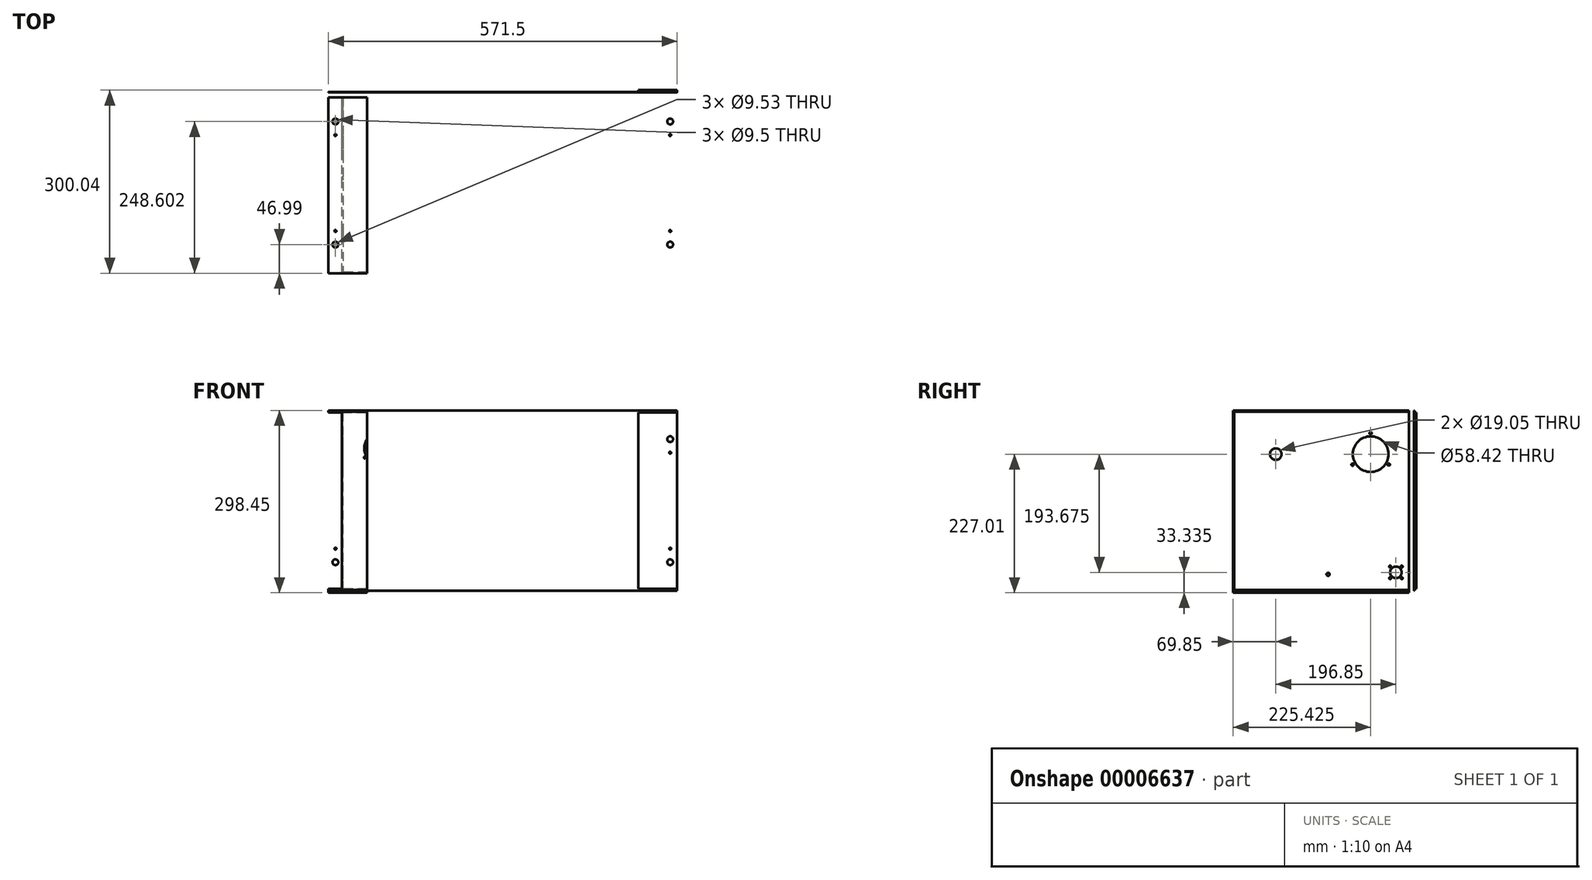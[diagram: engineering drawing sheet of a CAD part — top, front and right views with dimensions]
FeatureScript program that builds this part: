
annotation { "Feature Type Name" : "Feature", "Feature Type Description" : "" }
export const myFeature = defineFeature(function(context is Context, id is Id, definition is map)
    precondition{}
    {
        {
            var Q0;
            Q0=qCreatedBy(makeId("Top.planeOp"),FACE);
            var sketch = newSketch(context, id + "F0", { "sketchPlane" : qUnion([Q0])});
            skLineSegment(sketch, "E0", {"start": v(-263.53, 0) * mm, "end": v(263.53, 0) * mm});
            skLineSegment(sketch, "E1", {"start": v(-263.53, 0) * mm, "end": v(-263.53, 295.28) * mm});
            skLineSegment(sketch, "E2", {"start": v(-263.53, 295.28) * mm, "end": v(-262, 295.28) * mm});
            skLineSegment(sketch, "E3", {"start": v(-262, 295.28) * mm, "end": v(-262, 1.52) * mm});
            skLineSegment(sketch, "E4", {"start": v(-262, 1.52) * mm, "end": v(0, 1.52) * mm});
            skLineSegment(sketch, "E5", {"start": v(0, -110.06) * mm, "end": v(0, 345.42) * mm, "construction": true});
            skLineSegment(sketch, "E6.0.MirrorCS", {"start": v(262, 295.28) * mm, "end": v(262, 1.52) * mm});
            skLineSegment(sketch, "E6.1.MirrorCS", {"start": v(263.53, 0) * mm, "end": v(263.53, 295.28) * mm});
            skLineSegment(sketch, "E6.2.MirrorCS", {"start": v(262, 1.52) * mm, "end": v(0, 1.52) * mm});
            skLineSegment(sketch, "E6.3.MirrorCS", {"start": v(263.53, 295.28) * mm, "end": v(262, 295.28) * mm});
            skSolve(sketch);
        }
        {
            var Q0;
            Q0=makeQuery(id+"F0.imprint","IMPRINT",FACE,{"disambiguationData":[TD([[makeQuery(id+"F0.imprint","IMPRINT",EDGE,{"derivedFrom":sQuery(id+"F0.wireOp",EDGE,"E0")}),1.0]])]});
            var Q1;
            Q1=sQuery(id+"F0.wireOp",EDGE,"E3");
            extrude(context, id + "F1", {"entities" : qUnion([Q0]), "surfaceEntities" : qUnion([Q1]), "depth" : 292.1 * mm});
        }
        {
            var Q0;
            Q0=makeQuery(id+"F1.opExtrude","SWEPT_EDGE",EDGE,{"disambiguationData":[OSD([sQuery(id+"F0.wireOp",EDGE,"E0"),sQuery(id+"F0.wireOp",EDGE,"E1")])]});
            var Q1;
            Q1=makeQuery(id+"F1.opExtrude","CAP_EDGE",EDGE,{"disambiguationData":[OSD([sQuery(id+"F0.wireOp",EDGE,"E0")])],"isStart":true});
            var Q2;
            Q2=makeQuery(id+"F1.opExtrude","CAP_EDGE",EDGE,{"disambiguationData":[OSD([sQuery(id+"F0.wireOp",EDGE,"E1")])],"isStart":true});
            var Q3;
            Q3=makeQuery(id+"F1.opExtrude","SWEPT_EDGE",EDGE,{"disambiguationData":[OSD([sQuery(id+"F0.wireOp",EDGE,"E1"),sQuery(id+"F0.wireOp",EDGE,"E2")])]});
            var Q4;
            Q4=makeQuery(id+"F1.opExtrude","CAP_EDGE",EDGE,{"disambiguationData":[OSD([sQuery(id+"F0.wireOp",EDGE,"E1")])],"isStart":false});
            var Q5;
            Q5=makeQuery(id+"F1.opExtrude","CAP_EDGE",EDGE,{"disambiguationData":[OSD([sQuery(id+"F0.wireOp",EDGE,"E0")])],"isStart":false});
            var Q6;
            Q6=makeQuery(id+"F1.opExtrude","SWEPT_EDGE",EDGE,{"disambiguationData":[OSD([sQuery(id+"F0.wireOp",EDGE,"E0"),sQuery(id+"F0.wireOp",EDGE,"E6.1.MirrorCS")])]});
            var Q7;
            Q7=makeQuery(id+"F1.opExtrude","CAP_EDGE",EDGE,{"disambiguationData":[OSD([sQuery(id+"F0.wireOp",EDGE,"E6.1.MirrorCS")])],"isStart":false});
            var Q8;
            Q8=makeQuery(id+"F1.opExtrude","SWEPT_EDGE",EDGE,{"disambiguationData":[OSD([sQuery(id+"F0.wireOp",EDGE,"E6.1.MirrorCS"),sQuery(id+"F0.wireOp",EDGE,"E6.3.MirrorCS")])]});
            var Q9;
            Q9=makeQuery(id+"F1.opExtrude","CAP_EDGE",EDGE,{"disambiguationData":[OSD([sQuery(id+"F0.wireOp",EDGE,"E6.1.MirrorCS")])],"isStart":true});
            fillet(context, id + "F2", {"entities" : qUnion([Q0, Q1, Q2, Q3, Q4, Q5, Q6, Q7, Q8, Q9]), "radius" : 1.27 * mm, "tangentPropagation" : true, "allowEdgeOverflow" : false});
        }
        {
            var Q0;
            Q0=makeQuery(id+"F1.opExtrude","SWEPT_FACE",FACE,{"disambiguationData":[OSD([sQuery(id+"F0.wireOp",EDGE,"E0")])]});
            var sketch = newSketch(context, id + "F3", { "sketchPlane" : qUnion([Q0])});
            skLineSegment(sketch, "E7", {"start": v(0, -22.71) * mm, "end": v(0, 428.97) * mm, "construction": true});
            skLineSegment(sketch, "E8", {"start": v(-397, 0) * mm, "end": v(381.47, 0) * mm, "construction": true});
            skLineSegment(sketch, "E9", {"start": v(-394.87, 98.43) * mm, "end": v(382.18, 98.43) * mm, "construction": true});
            skLineSegment(sketch, "E10", {"start": v(-317.78, 107.95) * mm, "end": v(297.56, 107.95) * mm, "construction": true});
            skLineSegment(sketch, "E11", {"start": v(-291.05, 196.85) * mm, "end": v(299.62, 196.85) * mm, "construction": true});
            skLineSegment(sketch, "E12", {"start": v(-305.21, 231.77) * mm, "end": v(297.58, 231.78) * mm, "construction": true});
            skLineSegment(sketch, "E13", {"start": v(-200.02, 339.47) * mm, "end": v(-200.02, -33.8) * mm, "construction": true});
            skLineSegment(sketch, "E14", {"start": v(-161.92, 338.18) * mm, "end": v(-161.92, -31.85) * mm, "construction": true});
            skLineSegment(sketch, "E15", {"start": v(-122.24, 325.89) * mm, "end": v(-122.24, -26.68) * mm, "construction": true});
            skLineSegment(sketch, "E16", {"start": v(-66.68, 340.76) * mm, "end": v(-66.67, -29.91) * mm, "construction": true});
            skLineSegment(sketch, "E17", {"start": v(25.4, 334.3) * mm, "end": v(25.4, -17.62) * mm, "construction": true});
            skLineSegment(sketch, "E18", {"start": v(152.4, 322) * mm, "end": v(152.4, -46.73) * mm, "construction": true});
            skLineSegment(sketch, "E19", {"start": v(263.52, 358.39) * mm, "end": v(263.52, -46.4) * mm, "construction": true});
            skCircle(sketch, "E20", {"center": v(-200.02, 231.77) * mm, "radius": 26.99 * mm});
            skCircle(sketch, "E21", {"center": v(-200.02, 231.77) * mm, "radius": 30.16 * mm, "construction": true});
            skCircle(sketch, "E22", {"center": v(-200.02, 261.94) * mm, "radius": 1.63 * mm});
            skCircle(sketch, "E23.1.0", {"center": v(-226.15, 216.7) * mm, "radius": 1.63 * mm});
            skCircle(sketch, "E23.2.0", {"center": v(-173.9, 216.7) * mm, "radius": 1.63 * mm});
            skCircle(sketch, "E24", {"center": v(-161.92, 98.43) * mm, "radius": 3.18 * mm});
            skCircle(sketch, "E25", {"center": v(-122.24, 98.43) * mm, "radius": 3.18 * mm});
            skCircle(sketch, "E26", {"center": v(-66.68, 196.85) * mm, "radius": 3.18 * mm});
            skCircle(sketch, "E27", {"center": v(25.4, 107.95) * mm, "radius": 3.18 * mm});
            skCircle(sketch, "E28", {"center": v(152.4, 196.85) * mm, "radius": 3.18 * mm});
            skSolve(sketch);
        }
        {
            var Q0;
            Q0=makeQuery(id+"F3.imprint","IMPRINT",FACE,{"disambiguationData":[TD([[makeQuery(id+"F3.imprint","IMPRINT",EDGE,{"derivedFrom":sQuery(id+"F3.wireOp",EDGE,"E22")}),1.0]])]});
            var Q1;
            Q1=makeQuery(id+"F3.imprint","IMPRINT",FACE,{"disambiguationData":[TD([[makeQuery(id+"F3.imprint","IMPRINT",EDGE,{"derivedFrom":sQuery(id+"F3.wireOp",EDGE,"E20")}),1.0]])]});
            var Q2;
            Q2=makeQuery(id+"F3.imprint","IMPRINT",FACE,{"disambiguationData":[TD([[makeQuery(id+"F3.imprint","IMPRINT",EDGE,{"derivedFrom":sQuery(id+"F3.wireOp",EDGE,"E23.1.0")}),1.0]])]});
            var Q3;
            Q3=makeQuery(id+"F3.imprint","IMPRINT",FACE,{"disambiguationData":[TD([[makeQuery(id+"F3.imprint","IMPRINT",EDGE,{"derivedFrom":sQuery(id+"F3.wireOp",EDGE,"E23.2.0")}),1.0]])]});
            var Q4;
            Q4=makeQuery(id+"F3.imprint","IMPRINT",FACE,{"disambiguationData":[TD([[makeQuery(id+"F3.imprint","IMPRINT",EDGE,{"derivedFrom":sQuery(id+"F3.wireOp",EDGE,"E26")}),1.0]])]});
            var Q5;
            Q5=makeQuery(id+"F3.imprint","IMPRINT",FACE,{"disambiguationData":[TD([[makeQuery(id+"F3.imprint","IMPRINT",EDGE,{"derivedFrom":sQuery(id+"F3.wireOp",EDGE,"E24")}),1.0]])]});
            var Q6;
            Q6=makeQuery(id+"F3.imprint","IMPRINT",FACE,{"disambiguationData":[TD([[makeQuery(id+"F3.imprint","IMPRINT",EDGE,{"derivedFrom":sQuery(id+"F3.wireOp",EDGE,"E25")}),1.0]])]});
            var Q7;
            Q7=makeQuery(id+"F3.imprint","IMPRINT",FACE,{"disambiguationData":[TD([[makeQuery(id+"F3.imprint","IMPRINT",EDGE,{"derivedFrom":sQuery(id+"F3.wireOp",EDGE,"E27")}),1.0]])]});
            var Q8;
            Q8=makeQuery(id+"F3.imprint","IMPRINT",FACE,{"disambiguationData":[TD([[makeQuery(id+"F3.imprint","IMPRINT",EDGE,{"derivedFrom":sQuery(id+"F3.wireOp",EDGE,"E28")}),1.0]])]});
            extrude(context, id + "F4", {"entities" : qUnion([Q0, Q1, Q2, Q3, Q4, Q5, Q6, Q7, Q8]), "operationType" : NewBodyOperationType.REMOVE, "oppositeDirection" : true, "depth" : 5.08 * mm});
        }
        {
            var Q0;
            Q0=makeQuery(id+"F1.opExtrude","SWEPT_FACE",FACE,{"disambiguationData":[OSD([sQuery(id+"F0.wireOp",EDGE,"E1")])]});
            var sketch = newSketch(context, id + "F5", { "sketchPlane" : qUnion([Q0])});
            skLineSegment(sketch, "E29", {"start": v(-69.85, 280.52) * mm, "end": v(-69.85, -27.41) * mm, "construction": true});
            skLineSegment(sketch, "E30", {"start": v(-155.58, 281.42) * mm, "end": v(-155.58, -27.41) * mm, "construction": true});
            skLineSegment(sketch, "E31", {"start": v(-225.42, 273.8) * mm, "end": v(-225.42, -23.83) * mm, "construction": true});
            skLineSegment(sketch, "E32", {"start": v(-266.7, 273.35) * mm, "end": v(-266.7, -23.83) * mm, "construction": true});
            skLineSegment(sketch, "E33", {"start": v(-314.98, 222.25) * mm, "end": v(77.22, 222.25) * mm, "construction": true});
            skLineSegment(sketch, "E34", {"start": v(-285.84, 28.57) * mm, "end": v(55.7, 28.57) * mm, "construction": true});
            skLineSegment(sketch, "E35", {"start": v(-279.57, 25.4) * mm, "end": v(62.43, 25.4) * mm, "construction": true});
            skLineSegment(sketch, "E36", {"start": v(-294.95, 0) * mm, "end": v(40.89, 0) * mm, "construction": true});
            skLineSegment(sketch, "E37", {"start": v(0, -20.23) * mm, "end": v(0, 311.99) * mm, "construction": true});
            skCircle(sketch, "E38", {"center": v(-225.42, 222.25) * mm, "radius": 29.21 * mm});
            skCircle(sketch, "E39", {"center": v(-69.85, 222.25) * mm, "radius": 9.53 * mm});
            skCircle(sketch, "E40", {"center": v(-155.58, 25.4) * mm, "radius": 2.54 * mm});
            skCircle(sketch, "E41", {"center": v(-266.7, 28.57) * mm, "radius": 9.53 * mm});
            skCircle(sketch, "E42", {"center": v(-257.18, 38.1) * mm, "radius": 1.63 * mm});
            skCircle(sketch, "E43.0.1.0", {"center": v(-257.18, 19.05) * mm, "radius": 1.63 * mm});
            skCircle(sketch, "E43.1.0.0", {"center": v(-276.23, 38.1) * mm, "radius": 1.63 * mm});
            skCircle(sketch, "E43.1.1.0", {"center": v(-276.23, 19.05) * mm, "radius": 1.63 * mm});
            skLineSegment(sketch, "E43.direction1", {"start": v(-257.18, 38.1) * mm, "end": v(-276.23, 38.1) * mm, "construction": true});
            skLineSegment(sketch, "E43.direction2", {"start": v(-257.18, 38.1) * mm, "end": v(-257.18, 19.05) * mm, "construction": true});
            skCircle(sketch, "E44", {"center": v(-225.43, 256.54) * mm, "radius": 1.9 * mm});
            skCircle(sketch, "E45.1.0", {"center": v(-255.12, 205.1) * mm, "radius": 1.9 * mm});
            skCircle(sketch, "E45.2.0", {"center": v(-195.73, 205.1) * mm, "radius": 1.9 * mm});
            skSolve(sketch);
        }
        {
            var Q0;
            Q0=makeQuery(id+"F5.imprint","IMPRINT",FACE,{"disambiguationData":[TD([[makeQuery(id+"F5.imprint","IMPRINT",EDGE,{"derivedFrom":sQuery(id+"F5.wireOp",EDGE,"E44")}),1.0]])]});
            var Q1;
            Q1=makeQuery(id+"F5.imprint","IMPRINT",FACE,{"disambiguationData":[TD([[makeQuery(id+"F5.imprint","IMPRINT",EDGE,{"derivedFrom":sQuery(id+"F5.wireOp",EDGE,"E38")}),1.0]])]});
            var Q2;
            Q2=makeQuery(id+"F5.imprint","IMPRINT",FACE,{"disambiguationData":[TD([[makeQuery(id+"F5.imprint","IMPRINT",EDGE,{"derivedFrom":sQuery(id+"F5.wireOp",EDGE,"E45.1.0")}),1.0]])]});
            var Q3;
            Q3=makeQuery(id+"F5.imprint","IMPRINT",FACE,{"disambiguationData":[TD([[makeQuery(id+"F5.imprint","IMPRINT",EDGE,{"derivedFrom":sQuery(id+"F5.wireOp",EDGE,"E45.2.0")}),1.0]])]});
            var Q4;
            Q4=makeQuery(id+"F5.imprint","IMPRINT",FACE,{"disambiguationData":[TD([[makeQuery(id+"F5.imprint","IMPRINT",EDGE,{"derivedFrom":sQuery(id+"F5.wireOp",EDGE,"E39")}),1.0]])]});
            var Q5;
            Q5=makeQuery(id+"F5.imprint","IMPRINT",FACE,{"disambiguationData":[TD([[makeQuery(id+"F5.imprint","IMPRINT",EDGE,{"derivedFrom":sQuery(id+"F5.wireOp",EDGE,"E40")}),1.0]])]});
            var Q6;
            Q6=makeQuery(id+"F5.imprint","IMPRINT",FACE,{"disambiguationData":[TD([[makeQuery(id+"F5.imprint","IMPRINT",EDGE,{"derivedFrom":sQuery(id+"F5.wireOp",EDGE,"E41")}),1.0]])]});
            var Q7;
            Q7=makeQuery(id+"F5.imprint","IMPRINT",FACE,{"disambiguationData":[TD([[makeQuery(id+"F5.imprint","IMPRINT",EDGE,{"derivedFrom":sQuery(id+"F5.wireOp",EDGE,"E43.1.0.0")}),1.0]])]});
            var Q8;
            Q8=makeQuery(id+"F5.imprint","IMPRINT",FACE,{"disambiguationData":[TD([[makeQuery(id+"F5.imprint","IMPRINT",EDGE,{"derivedFrom":sQuery(id+"F5.wireOp",EDGE,"E43.1.1.0")}),1.0]])]});
            var Q9;
            Q9=makeQuery(id+"F5.imprint","IMPRINT",FACE,{"disambiguationData":[TD([[makeQuery(id+"F5.imprint","IMPRINT",EDGE,{"derivedFrom":sQuery(id+"F5.wireOp",EDGE,"E43.0.1.0")}),1.0]])]});
            var Q10;
            Q10=makeQuery(id+"F5.imprint","IMPRINT",FACE,{"disambiguationData":[TD([[makeQuery(id+"F5.imprint","IMPRINT",EDGE,{"derivedFrom":sQuery(id+"F5.wireOp",EDGE,"E42")}),1.0]])]});
            extrude(context, id + "F6", {"entities" : qUnion([Q0, Q1, Q2, Q3, Q4, Q5, Q6, Q7, Q8, Q9, Q10]), "operationType" : NewBodyOperationType.REMOVE, "oppositeDirection" : true, "depth" : 5.08 * mm});
        }
        {
            var Q0;
            Q0=makeQuery(id+"F1.opExtrude","SWEPT_FACE",FACE,{"disambiguationData":[OSD([sQuery(id+"F0.wireOp",EDGE,"E6.1.MirrorCS")])]});
            var sketch = newSketch(context, id + "F7", { "sketchPlane" : qUnion([Q0])});
            skLineSegment(sketch, "E46", {"start": v(-61.82, 0) * mm, "end": v(412.73, 0) * mm, "construction": true});
            skLineSegment(sketch, "E47", {"start": v(0, -19.8) * mm, "end": v(0, 392.1) * mm, "construction": true});
            skLineSegment(sketch, "E48", {"start": v(-42.4, 193.68) * mm, "end": v(431.33, 193.68) * mm, "construction": true});
            skLineSegment(sketch, "E49", {"start": v(-58.3, 38.1) * mm, "end": v(354.8, 38.1) * mm, "construction": true});
            skLineSegment(sketch, "E50", {"start": v(34.92, 306) * mm, "end": v(34.93, -19.24) * mm, "construction": true});
            skLineSegment(sketch, "E51", {"start": v(107.95, 307.86) * mm, "end": v(107.95, -22.5) * mm, "construction": true});
            skLineSegment(sketch, "E52", {"start": v(171.45, 313.59) * mm, "end": v(171.45, -34.35) * mm, "construction": true});
            skArc(sketch, "E53", {"start": v(107.95, 257.18) * mm, "mid": v(44.45, 193.68) * mm, "end": v(107.95, 130.18) * mm});
            skCircle(sketch, "E54", {"center": v(34.93, 38.1) * mm, "radius": 7.94 * mm});
            skCircle(sketch, "E55", {"center": v(44.13, 47.3) * mm, "radius": 1.63 * mm});
            skCircle(sketch, "E56.0.1.0", {"center": v(44.13, 29.53) * mm, "radius": 1.63 * mm});
            skCircle(sketch, "E56.1.0.0", {"center": v(26.35, 47.3) * mm, "radius": 1.63 * mm});
            skCircle(sketch, "E56.1.1.0", {"center": v(26.35, 29.53) * mm, "radius": 1.63 * mm});
            skLineSegment(sketch, "E56.direction1", {"start": v(44.13, 47.3) * mm, "end": v(26.35, 47.3) * mm, "construction": true});
            skLineSegment(sketch, "E56.direction2", {"start": v(44.13, 47.3) * mm, "end": v(44.13, 29.53) * mm, "construction": true});
            skLineSegment(sketch, "E57", {"start": v(107.95, 257.18) * mm, "end": v(171.45, 257.18) * mm});
            skLineSegment(sketch, "E58", {"start": v(107.95, 130.18) * mm, "end": v(171.45, 130.18) * mm});
            skArc(sketch, "E59.trimOffspring", {"start": v(171.45, 130.18) * mm, "mid": v(234.95, 193.68) * mm, "end": v(171.45, 257.18) * mm});
            skSolve(sketch);
        }
        {
            var Q0;
            Q0=makeQuery(id+"F7.imprint","IMPRINT",FACE,{"disambiguationData":[TD([[makeQuery(id+"F7.imprint","IMPRINT",EDGE,{"derivedFrom":sQuery(id+"F7.wireOp",EDGE,"E53")}),1.0]])]});
            var Q1;
            Q1=makeQuery(id+"F7.imprint","IMPRINT",FACE,{"disambiguationData":[TD([[makeQuery(id+"F7.imprint","IMPRINT",EDGE,{"derivedFrom":sQuery(id+"F7.wireOp",EDGE,"E56.1.0.0")}),1.0]])]});
            var Q2;
            Q2=makeQuery(id+"F7.imprint","IMPRINT",FACE,{"disambiguationData":[TD([[makeQuery(id+"F7.imprint","IMPRINT",EDGE,{"derivedFrom":sQuery(id+"F7.wireOp",EDGE,"E55")}),1.0]])]});
            var Q3;
            Q3=makeQuery(id+"F7.imprint","IMPRINT",FACE,{"disambiguationData":[TD([[makeQuery(id+"F7.imprint","IMPRINT",EDGE,{"derivedFrom":sQuery(id+"F7.wireOp",EDGE,"E56.0.1.0")}),1.0]])]});
            var Q4;
            Q4=makeQuery(id+"F7.imprint","IMPRINT",FACE,{"disambiguationData":[TD([[makeQuery(id+"F7.imprint","IMPRINT",EDGE,{"derivedFrom":sQuery(id+"F7.wireOp",EDGE,"E56.1.1.0")}),1.0]])]});
            var Q5;
            Q5=makeQuery(id+"F7.imprint","IMPRINT",FACE,{"disambiguationData":[TD([[makeQuery(id+"F7.imprint","IMPRINT",EDGE,{"derivedFrom":sQuery(id+"F7.wireOp",EDGE,"E54")}),1.0]])]});
            extrude(context, id + "F8", {"entities" : qUnion([Q0, Q1, Q2, Q3, Q4, Q5]), "operationType" : NewBodyOperationType.REMOVE, "oppositeDirection" : true, "depth" : 5.08 * mm});
        }
        {
            var Q0;
            Q0=qCreatedBy(makeId("Right.planeOp"),FACE);
            var sketch = newSketch(context, id + "F9", { "sketchPlane" : qUnion([Q0])});
            skLineSegment(sketch, "E60", {"start": v(-28.58, 0) * mm, "end": v(311.73, 0) * mm, "construction": true});
            skLineSegment(sketch, "E61", {"start": v(0, -27.06) * mm, "end": v(0, 319.24) * mm, "construction": true});
            skLineSegment(sketch, "E62", {"start": v(0, 0) * mm, "end": v(295.28, 0) * mm});
            skLineSegment(sketch, "E63", {"start": v(295.28, 0) * mm, "end": v(295.28, 292.1) * mm});
            skLineSegment(sketch, "E64", {"start": v(295.27, 292.1) * mm, "end": v(0, 292.1) * mm});
            skLineSegment(sketch, "E65", {"start": v(0, 292.1) * mm, "end": v(0, 293.69) * mm});
            skLineSegment(sketch, "E66", {"start": v(0, 293.69) * mm, "end": v(296.35, 293.69) * mm});
            skLineSegment(sketch, "E67", {"start": v(296.86, 293.18) * mm, "end": v(296.86, -1.08) * mm});
            skLineSegment(sketch, "E68", {"start": v(296.35, -1.59) * mm, "end": v(0, -1.59) * mm});
            skLineSegment(sketch, "E69", {"start": v(0, -1.59) * mm, "end": v(0, 0) * mm});
            skPoint(sketch, "E70.visualSharp", {"position": v(296.86, 293.69) * mm});
            skArc(sketch, "E70.filletArc", {"start": v(296.86, 293.18) * mm, "mid": v(296.71, 293.54) * mm, "end": v(296.35, 293.69) * mm});
            skPoint(sketch, "E71.visualSharp", {"position": v(296.86, -1.59) * mm});
            skArc(sketch, "E71.filletArc", {"start": v(296.35, -1.59) * mm, "mid": v(296.71, -1.44) * mm, "end": v(296.86, -1.08) * mm});
            skSolve(sketch);
        }
        {
            var Q0;
            Q0=makeQuery(id+"F9.imprint","IMPRINT",FACE,{"disambiguationData":[TD([[makeQuery(id+"F9.imprint","IMPRINT",EDGE,{"derivedFrom":sQuery(id+"F9.wireOp",EDGE,"E62")}),-1.0]])]});
            extrude(context, id + "F10", {"entities" : qUnion([Q0]), "endBound" : BoundingType.SYMMETRIC, "depth" : 571.5 * mm});
        }
        {
            var Q0;
            Q0=makeQuery(id+"F1.opExtrude","SWEPT_FACE",FACE,{"disambiguationData":[OSD([sQuery(id+"F0.wireOp",EDGE,"E6.0.MirrorCS")])]});
            var sketch = newSketch(context, id + "F11", { "sketchPlane" : qUnion([Q0])});
            skLineSegment(sketch, "E72", {"start": v(-139.7, 257.18) * mm, "end": v(-139.7, 130.18) * mm, "construction": true});
            skLineSegment(sketch, "E73.rect.bottom", {"start": v(-254, 269.88) * mm, "end": v(-25.4, 269.88) * mm});
            skLineSegment(sketch, "E73.rect.top", {"start": v(-254, 117.48) * mm, "end": v(-25.4, 117.48) * mm});
            skLineSegment(sketch, "E73.rect.left", {"start": v(-254, 269.88) * mm, "end": v(-254, 117.48) * mm});
            skLineSegment(sketch, "E73.rect.right", {"start": v(-25.4, 269.88) * mm, "end": v(-25.4, 117.48) * mm});
            skPoint(sketch, "E73.rect.middle", {"position": v(-139.7, 193.68) * mm});
            skCircle(sketch, "E74", {"center": v(-177.8, 193.68) * mm, "radius": 3.18 * mm});
            skLineSegment(sketch, "E75", {"start": v(-61.04, 193.68) * mm, "end": v(-209.95, 193.68) * mm, "construction": true});
            skCircle(sketch, "E76.0.MirrorC", {"center": v(-101.6, 193.68) * mm, "radius": 3.18 * mm});
            skSolve(sketch);
        }
        {
            var Q0;
            Q0=makeQuery(id+"F11.imprint","IMPRINT",FACE,{"disambiguationData":[TD([[makeQuery(id+"F11.imprint","IMPRINT",EDGE,{"derivedFrom":sQuery(id+"F11.wireOp",EDGE,"E73.rect.bottom")}),-1.0]])]});
            var Q1;
            Q1=makeQuery(id+"F11.imprint","IMPRINT",FACE,{"disambiguationData":[TD([[makeQuery(id+"F11.imprint","IMPRINT",EDGE,{"derivedFrom":sQuery(id+"F11.wireOp",EDGE,"E74")}),-1.0]])]});
            extrude(context, id + "F12", {"entities" : qUnion([Q0, Q1]), "depth" : 3.17 * mm});
        }
        {
            var Q0;
            Q0=makeQuery(id+"F10.opExtrude","SWEPT_FACE",FACE,{"disambiguationData":[OSD([sQuery(id+"F9.wireOp",EDGE,"E68")])]});
            var sketch = newSketch(context, id + "F13", { "sketchPlane" : qUnion([Q0])});
            skLineSegment(sketch, "E77", {"start": v(-285.75, 3.7) * mm, "end": v(-285.75, -308.75) * mm, "construction": true});
            skLineSegment(sketch, "E78", {"start": v(-292.16, 0) * mm, "end": v(-252.35, 0) * mm, "construction": true});
            skLineSegment(sketch, "E79", {"start": v(0, 19.92) * mm, "end": v(0, -311.68) * mm, "construction": true});
            skLineSegment(sketch, "E80", {"start": v(-274.32, 41.27) * mm, "end": v(-274.32, -317.65) * mm, "construction": true});
            skCircle(sketch, "E81", {"center": v(-274.32, -46.99) * mm, "radius": 4.76 * mm});
            skCircle(sketch, "E82", {"center": v(-274.32, -69.21) * mm, "radius": 1.59 * mm});
            skCircle(sketch, "E83", {"center": v(-274.32, -248.6) * mm, "radius": 4.75 * mm});
            skCircle(sketch, "E84", {"center": v(-274.32, -226.38) * mm, "radius": 1.59 * mm});
            skCircle(sketch, "E85.0.MirrorC", {"center": v(274.32, -46.99) * mm, "radius": 4.76 * mm});
            skCircle(sketch, "E85.1.MirrorC", {"center": v(274.32, -69.21) * mm, "radius": 1.59 * mm});
            skCircle(sketch, "E85.2.MirrorC", {"center": v(274.32, -248.6) * mm, "radius": 4.75 * mm});
            skCircle(sketch, "E85.3.MirrorC", {"center": v(274.32, -226.38) * mm, "radius": 1.59 * mm});
            skLineSegment(sketch, "E86.bottom", {"start": v(-285.75, 0) * mm, "end": v(-222.25, 0) * mm});
            skLineSegment(sketch, "E86.top", {"start": v(-285.75, -287.88) * mm, "end": v(-222.25, -287.88) * mm});
            skLineSegment(sketch, "E86.left", {"start": v(-285.75, 0) * mm, "end": v(-285.75, -287.88) * mm});
            skLineSegment(sketch, "E86.right", {"start": v(-222.25, 0) * mm, "end": v(-222.25, -287.88) * mm});
            skSolve(sketch);
        }
        {
            var Q0;
            Q0=makeQuery(id+"F13.imprint","IMPRINT",FACE,{"disambiguationData":[TD([[makeQuery(id+"F13.imprint","IMPRINT",EDGE,{"derivedFrom":sQuery(id+"F13.wireOp",EDGE,"E81")}),1.0]])]});
            var Q1;
            Q1=makeQuery(id+"F13.imprint","IMPRINT",FACE,{"disambiguationData":[TD([[makeQuery(id+"F13.imprint","IMPRINT",EDGE,{"derivedFrom":sQuery(id+"F13.wireOp",EDGE,"E82")}),1.0]])]});
            var Q2;
            Q2=makeQuery(id+"F13.imprint","IMPRINT",FACE,{"disambiguationData":[TD([[makeQuery(id+"F13.imprint","IMPRINT",EDGE,{"derivedFrom":sQuery(id+"F13.wireOp",EDGE,"E84")}),1.0]])]});
            var Q3;
            Q3=makeQuery(id+"F13.imprint","IMPRINT",FACE,{"disambiguationData":[TD([[makeQuery(id+"F13.imprint","IMPRINT",EDGE,{"derivedFrom":sQuery(id+"F13.wireOp",EDGE,"E83")}),1.0]])]});
            var Q4;
            Q4=makeQuery(id+"F13.imprint","IMPRINT",FACE,{"disambiguationData":[TD([[makeQuery(id+"F13.imprint","IMPRINT",EDGE,{"derivedFrom":sQuery(id+"F13.wireOp",EDGE,"E85.3.MirrorC")}),-1.0]])]});
            var Q5;
            Q5=makeQuery(id+"F13.imprint","IMPRINT",FACE,{"disambiguationData":[TD([[makeQuery(id+"F13.imprint","IMPRINT",EDGE,{"derivedFrom":sQuery(id+"F13.wireOp",EDGE,"E85.2.MirrorC")}),-1.0]])]});
            var Q6;
            Q6=makeQuery(id+"F13.imprint","IMPRINT",FACE,{"disambiguationData":[TD([[makeQuery(id+"F13.imprint","IMPRINT",EDGE,{"derivedFrom":sQuery(id+"F13.wireOp",EDGE,"E85.0.MirrorC")}),-1.0]])]});
            var Q7;
            Q7=makeQuery(id+"F13.imprint","IMPRINT",FACE,{"disambiguationData":[TD([[makeQuery(id+"F13.imprint","IMPRINT",EDGE,{"derivedFrom":sQuery(id+"F13.wireOp",EDGE,"E85.1.MirrorC")}),-1.0]])]});
            extrude(context, id + "F14", {"entities" : qUnion([Q0, Q1, Q2, Q3, Q4, Q5, Q6, Q7]), "operationType" : NewBodyOperationType.REMOVE, "oppositeDirection" : true, "depth" : 317.5 * mm});
        }
        {
            var Q0;
            Q0 = qSketchRegion(id + "F13", true);
            extrude(context, id + "F15", {"entities" : qUnion([Q0]), "depth" : 3.17 * mm});
        }
        {
            var Q0;
            Q0=makeQuery(id+"F15.opExtrude","SWEPT_BODY",BODY,{"disambiguationData":[OSD([sQuery(id+"F13.wireOp",EDGE,"E85.0.MirrorC")])]});
            deleteBodies(context, id + "F16", {"entities" : qUnion([Q0])});
        }
        {
            var Q0;
            Q0=makeQuery(id+"F15.opExtrude","SWEPT_BODY",BODY,{"disambiguationData":[OSD([sQuery(id+"F13.wireOp",EDGE,"E85.1.MirrorC")])]});
            deleteBodies(context, id + "F17", {"entities" : qUnion([Q0])});
        }
        {
            var Q0;
            Q0=makeQuery(id+"F15.opExtrude","SWEPT_BODY",BODY,{"disambiguationData":[OSD([sQuery(id+"F13.wireOp",EDGE,"E85.2.MirrorC")])]});
            deleteBodies(context, id + "F18", {"entities" : qUnion([Q0])});
        }
        {
            var Q0;
            Q0=makeQuery(id+"F15.opExtrude","SWEPT_BODY",BODY,{"disambiguationData":[OSD([sQuery(id+"F13.wireOp",EDGE,"E85.3.MirrorC")])]});
            deleteBodies(context, id + "F19", {"entities" : qUnion([Q0])});
        }
        {
            var Q0;
            Q0=makeQuery(id+"F10.opExtrude","SWEPT_FACE",FACE,{"disambiguationData":[OSD([sQuery(id+"F9.wireOp",EDGE,"E67")])]});
            var sketch = newSketch(context, id + "F20", { "sketchPlane" : qUnion([Q0])});
            skLineSegment(sketch, "E87", {"start": v(271.34, 0) * mm, "end": v(271.34, 292.1) * mm, "construction": true});
            skLineSegment(sketch, "E88", {"start": v(271.34, 146.05) * mm, "end": v(-316.6, 146.05) * mm, "construction": true});
            skLineSegment(sketch, "E89", {"start": v(0, -37.93) * mm, "end": v(0, 353.23) * mm, "construction": true});
            skLineSegment(sketch, "E90", {"start": v(-285.75, 295.46) * mm, "end": v(-285.75, -32.55) * mm, "construction": true});
            skLineSegment(sketch, "E91.rect.bottom", {"start": v(-285.75, 1.59) * mm, "end": v(-222.25, 1.59) * mm});
            skLineSegment(sketch, "E91.rect.top", {"start": v(-285.75, 290.51) * mm, "end": v(-222.25, 290.51) * mm});
            skLineSegment(sketch, "E91.rect.left", {"start": v(-285.75, 1.59) * mm, "end": v(-285.75, 290.51) * mm});
            skLineSegment(sketch, "E91.rect.right", {"start": v(-222.25, 1.59) * mm, "end": v(-222.25, 290.51) * mm});
            skPoint(sketch, "E91.rect.middle", {"position": v(-254, 146.05) * mm});
            skLineSegment(sketch, "E92", {"start": v(-274.32, -25.37) * mm, "end": v(-274.32, 327.88) * mm, "construction": true});
            skCircle(sketch, "E93", {"center": v(-274.32, 45.24) * mm, "radius": 4.75 * mm});
            skCircle(sketch, "E94", {"center": v(-274.32, 67.47) * mm, "radius": 1.59 * mm});
            skCircle(sketch, "E95.0.MirrorC", {"center": v(-274.32, 246.86) * mm, "radius": 4.75 * mm});
            skCircle(sketch, "E96.0.MirrorC", {"center": v(-274.32, 224.63) * mm, "radius": 1.59 * mm});
            skCircle(sketch, "E97.0.MirrorC", {"center": v(274.32, 246.86) * mm, "radius": 4.75 * mm});
            skCircle(sketch, "E97.1.MirrorC", {"center": v(274.32, 45.24) * mm, "radius": 4.75 * mm});
            skCircle(sketch, "E97.2.MirrorC", {"center": v(274.32, 224.63) * mm, "radius": 1.59 * mm});
            skCircle(sketch, "E97.3.MirrorC", {"center": v(274.32, 67.47) * mm, "radius": 1.59 * mm});
            skLineSegment(sketch, "E97.4.MirrorCS", {"start": v(285.75, 1.59) * mm, "end": v(285.75, 290.51) * mm});
            skLineSegment(sketch, "E97.5.MirrorCS", {"start": v(285.75, 1.59) * mm, "end": v(222.25, 1.59) * mm});
            skLineSegment(sketch, "E97.6.MirrorCS", {"start": v(222.25, 1.59) * mm, "end": v(222.25, 290.51) * mm});
            skLineSegment(sketch, "E97.7.MirrorCS", {"start": v(285.75, 290.51) * mm, "end": v(222.25, 290.51) * mm});
            skPoint(sketch, "E97.8.MirrorP", {"position": v(254, 146.05) * mm});
            skSolve(sketch);
        }
        {
            var Q0;
            Q0=makeQuery(id+"F20.imprint","IMPRINT",FACE,{"disambiguationData":[TD([[makeQuery(id+"F20.imprint","IMPRINT",EDGE,{"derivedFrom":sQuery(id+"F20.wireOp",EDGE,"E95.0.MirrorC")}),-1.0]])]});
            var Q1;
            Q1=makeQuery(id+"F20.imprint","IMPRINT",FACE,{"disambiguationData":[TD([[makeQuery(id+"F20.imprint","IMPRINT",EDGE,{"derivedFrom":sQuery(id+"F20.wireOp",EDGE,"E96.0.MirrorC")}),-1.0]])]});
            var Q2;
            Q2=makeQuery(id+"F20.imprint","IMPRINT",FACE,{"disambiguationData":[TD([[makeQuery(id+"F20.imprint","IMPRINT",EDGE,{"derivedFrom":sQuery(id+"F20.wireOp",EDGE,"E94")}),1.0]])]});
            var Q3;
            Q3=makeQuery(id+"F20.imprint","IMPRINT",FACE,{"disambiguationData":[TD([[makeQuery(id+"F20.imprint","IMPRINT",EDGE,{"derivedFrom":sQuery(id+"F20.wireOp",EDGE,"E93")}),1.0]])]});
            var Q4;
            Q4=makeQuery(id+"F20.imprint","IMPRINT",FACE,{"disambiguationData":[TD([[makeQuery(id+"F20.imprint","IMPRINT",EDGE,{"derivedFrom":sQuery(id+"F20.wireOp",EDGE,"E97.1.MirrorC")}),-1.0]])]});
            var Q5;
            Q5=makeQuery(id+"F20.imprint","IMPRINT",FACE,{"disambiguationData":[TD([[makeQuery(id+"F20.imprint","IMPRINT",EDGE,{"derivedFrom":sQuery(id+"F20.wireOp",EDGE,"E97.3.MirrorC")}),-1.0]])]});
            var Q6;
            Q6=makeQuery(id+"F20.imprint","IMPRINT",FACE,{"disambiguationData":[TD([[makeQuery(id+"F20.imprint","IMPRINT",EDGE,{"derivedFrom":sQuery(id+"F20.wireOp",EDGE,"E97.0.MirrorC")}),1.0]])]});
            var Q7;
            Q7=makeQuery(id+"F20.imprint","IMPRINT",FACE,{"disambiguationData":[TD([[makeQuery(id+"F20.imprint","IMPRINT",EDGE,{"derivedFrom":sQuery(id+"F20.wireOp",EDGE,"E97.2.MirrorC")}),1.0]])]});
            extrude(context, id + "F21", {"entities" : qUnion([Q0, Q1, Q2, Q3, Q4, Q5, Q6, Q7]), "operationType" : NewBodyOperationType.REMOVE, "oppositeDirection" : true, "depth" : 6.35 * mm});
        }
        {
            var Q0;
            Q0=makeQuery(id+"F20.imprint","IMPRINT",FACE,{"disambiguationData":[TD([[makeQuery(id+"F20.imprint","IMPRINT",EDGE,{"derivedFrom":sQuery(id+"F20.wireOp",EDGE,"E91.rect.bottom")}),1.0]])]});
            extrude(context, id + "F22", {"entities" : qUnion([Q0]), "depth" : 3.17 * mm});
        }
    });
